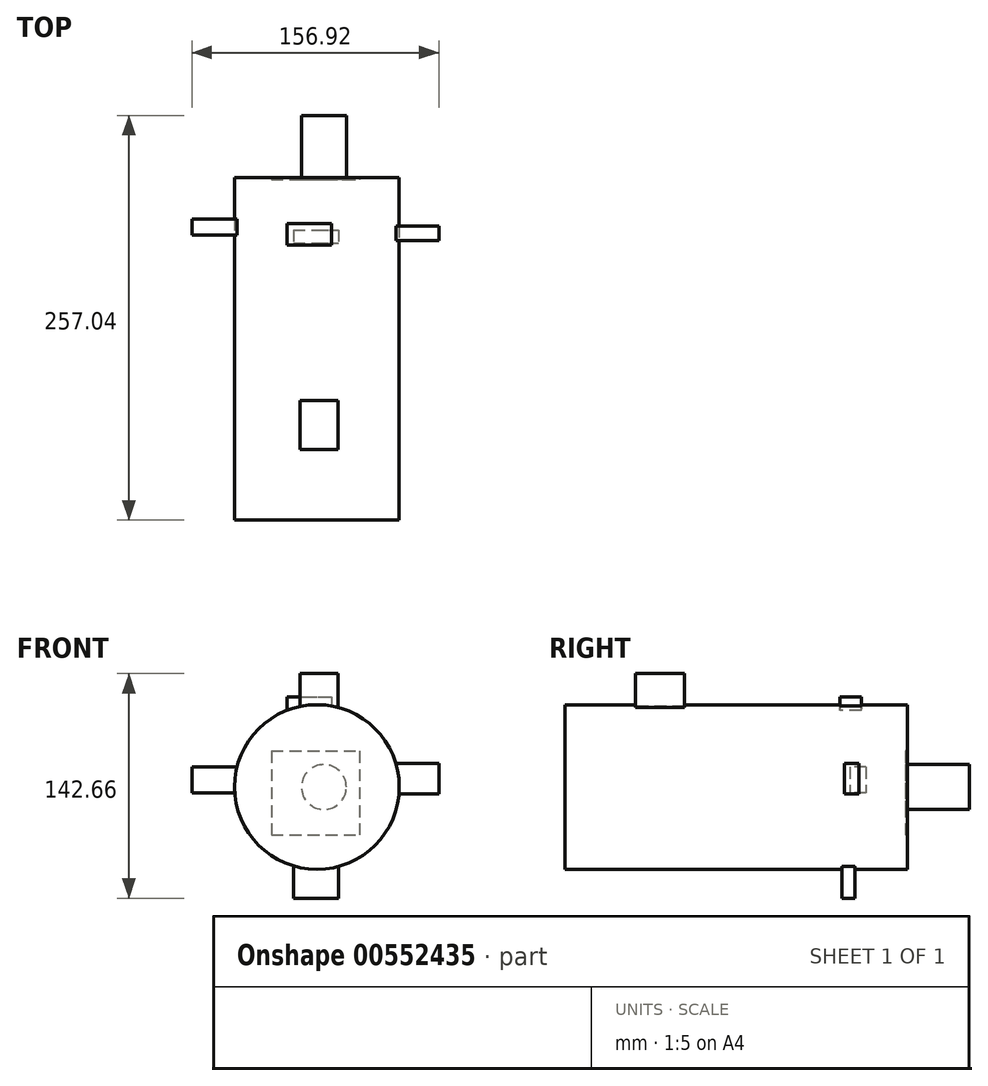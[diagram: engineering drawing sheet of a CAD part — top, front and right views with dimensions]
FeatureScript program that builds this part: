
annotation { "Feature Type Name" : "Feature", "Feature Type Description" : "" }
export const myFeature = defineFeature(function(context is Context, id is Id, definition is map)
    precondition{}
    {
        {
            var Q0;
            Q0=qCreatedBy(makeId("Front.planeOp"),FACE);
            var sketch = newSketch(context, id + "F0", { "sketchPlane" : qUnion([Q0])});
            skLineSegment(sketch, "E0.bottom", {"start": v(-9.91, 22.8) * mm, "end": v(46.17, 22.8) * mm});
            skLineSegment(sketch, "E0.top", {"start": v(-9.91, -30.45) * mm, "end": v(46.17, -30.45) * mm});
            skLineSegment(sketch, "E0.left", {"start": v(-9.91, 22.8) * mm, "end": v(-9.91, -30.45) * mm});
            skLineSegment(sketch, "E0.right", {"start": v(46.17, 22.8) * mm, "end": v(46.17, -30.45) * mm});
            skSolve(sketch);
        }
        {
            var Q0;
            Q0 = qSketchRegion(id + "F0", true);
            extrude(context, id + "F1", {"entities" : qUnion([Q0]), "depth" : 44.7 * mm, "offsetDistance" : 25.4 * mm});
        }
        {
            var Q0;
            Q0=makeQuery(id+"F1.opExtrude","CAP_FACE",FACE,{"disambiguationData":[OSD([sQuery(id+"F0.wireOp",EDGE,"E0.bottom"),sQuery(id+"F0.wireOp",EDGE,"E0.top"),sQuery(id+"F0.wireOp",EDGE,"E0.left"),sQuery(id+"F0.wireOp",EDGE,"E0.right")])],"isStart":true});
            extrude(context, id + "F2", {"entities" : qUnion([Q0]), "operationType" : NewBodyOperationType.ADD, "depth" : 156.46 * mm, "offsetDistance" : 25.4 * mm});
        }
        {
            var Q0;
            {var subQ0=sQuery(id+"F0.wireOp",EDGE,"E0.bottom");Q0=makeQuery(id+"F2.boolean.opBoolean","MERGE",FACE,{"derivedFrom":[makeQuery(id+"F1.opExtrude","SWEPT_FACE",FACE,{"disambiguationData":[OSD([subQ0])]}),makeQuery(id+"F2.opExtrude","SWEPT_FACE",FACE,{"disambiguationData":[OSD([subQ0])]})]});}
            var sketch = newSketch(context, id + "F3", { "sketchPlane" : qUnion([Q0])});
            skLineSegment(sketch, "E1", {"start": v(32.43, 0) * mm, "end": v(8.22, 0) * mm});
            skLineSegment(sketch, "E2", {"start": v(8.22, 0) * mm, "end": v(8.22, 31.27) * mm});
            skLineSegment(sketch, "E3", {"start": v(8.22, 31.27) * mm, "end": v(32.43, 31.27) * mm});
            skLineSegment(sketch, "E4", {"start": v(32.43, 31.27) * mm, "end": v(32.43, 0) * mm});
            skSolve(sketch);
        }
        {
            var Q0;
            Q0 = qSketchRegion(id + "F3", true);
            extrude(context, id + "F4", {"entities" : qUnion([Q0]), "operationType" : NewBodyOperationType.ADD, "depth" : 49.28 * mm, "offsetDistance" : 25.4 * mm});
        }
        {
            var Q0;
            Q0=makeQuery(id+"F1.opExtrude","CAP_FACE",FACE,{"disambiguationData":[OSD([sQuery(id+"F0.wireOp",EDGE,"E0.bottom"),sQuery(id+"F0.wireOp",EDGE,"E0.top"),sQuery(id+"F0.wireOp",EDGE,"E0.left"),sQuery(id+"F0.wireOp",EDGE,"E0.right")])],"isStart":false});
            var sketch = newSketch(context, id + "F5", { "sketchPlane" : qUnion([Q0])});
            skCircle(sketch, "E5", {"center": v(18.98, 0) * mm, "radius": 52.3 * mm});
            skSolve(sketch);
        }
        {
            var Q0;
            Q0 = qSketchRegion(id + "F5", true);
            extrude(context, id + "F6", {"entities" : qUnion([Q0]), "operationType" : NewBodyOperationType.ADD, "oppositeDirection" : true, "depth" : 167.39 * mm, "offsetDistance" : 25.4 * mm});
        }
        {
            var Q0;
            {var subQ0=sQuery(id+"F0.wireOp",EDGE,"E0.bottom");Q0=makeQuery(id+"F2.boolean.opBoolean","MERGE",FACE,{"derivedFrom":[makeQuery(id+"F1.opExtrude","SWEPT_FACE",FACE,{"disambiguationData":[OSD([subQ0])]}),makeQuery(id+"F2.opExtrude","SWEPT_FACE",FACE,{"disambiguationData":[OSD([subQ0])]})]});}
            var sketch = newSketch(context, id + "F7", { "sketchPlane" : qUnion([Q0])});
            skLineSegment(sketch, "E6.bottom", {"start": v(0, 143.52) * mm, "end": v(28.28, 143.52) * mm});
            skLineSegment(sketch, "E6.top", {"start": v(0, 130.11) * mm, "end": v(28.28, 130.11) * mm});
            skLineSegment(sketch, "E6.left", {"start": v(0, 143.52) * mm, "end": v(0, 130.11) * mm});
            skLineSegment(sketch, "E6.right", {"start": v(28.28, 143.52) * mm, "end": v(28.28, 130.11) * mm});
            skSolve(sketch);
        }
        {
            var Q0;
            Q0 = qSketchRegion(id + "F7", true);
            extrude(context, id + "F8", {"entities" : qUnion([Q0]), "operationType" : NewBodyOperationType.ADD, "depth" : 34.3 * mm, "offsetDistance" : 25.4 * mm});
        }
        {
            var Q0;
            {var subQ0=sQuery(id+"F0.wireOp",EDGE,"E0.right");Q0=makeQuery(id+"F2.boolean.opBoolean","MERGE",FACE,{"derivedFrom":[makeQuery(id+"F1.opExtrude","SWEPT_FACE",FACE,{"disambiguationData":[OSD([subQ0])]}),makeQuery(id+"F2.opExtrude","SWEPT_FACE",FACE,{"disambiguationData":[OSD([subQ0])]})]});}
            var sketch = newSketch(context, id + "F9", { "sketchPlane" : qUnion([Q0])});
            skLineSegment(sketch, "E7.bottom", {"start": v(142.1, 14.87) * mm, "end": v(132.75, 14.87) * mm});
            skLineSegment(sketch, "E7.top", {"start": v(142.1, -4.39) * mm, "end": v(132.75, -4.39) * mm});
            skLineSegment(sketch, "E7.left", {"start": v(142.1, 14.87) * mm, "end": v(142.1, -4.39) * mm});
            skLineSegment(sketch, "E7.right", {"start": v(132.75, 14.87) * mm, "end": v(132.75, -4.39) * mm});
            skSolve(sketch);
        }
        {
            var Q0;
            Q0 = qSketchRegion(id + "F9", true);
            extrude(context, id + "F10", {"entities" : qUnion([Q0]), "operationType" : NewBodyOperationType.ADD, "depth" : 50.3 * mm, "offsetDistance" : 25.4 * mm});
        }
        {
            var Q0;
            {var subQ0=sQuery(id+"F0.wireOp",EDGE,"E0.left");Q0=makeQuery(id+"F2.boolean.opBoolean","MERGE",FACE,{"derivedFrom":[makeQuery(id+"F1.opExtrude","SWEPT_FACE",FACE,{"disambiguationData":[OSD([subQ0])]}),makeQuery(id+"F2.opExtrude","SWEPT_FACE",FACE,{"disambiguationData":[OSD([subQ0])]})]});}
            var sketch = newSketch(context, id + "F11", { "sketchPlane" : qUnion([Q0])});
            skPoint(sketch, "E8.oppositeSnap0", {"position": v(-156.46, -3.82) * mm});
            skLineSegment(sketch, "E8.bottom", {"start": v(-136.37, 12.76) * mm, "end": v(-146.63, 12.76) * mm});
            skLineSegment(sketch, "E8.top", {"start": v(-136.37, -3.82) * mm, "end": v(-146.63, -3.82) * mm});
            skLineSegment(sketch, "E8.left", {"start": v(-136.37, 12.76) * mm, "end": v(-136.37, -3.82) * mm});
            skLineSegment(sketch, "E8.right", {"start": v(-146.63, 12.76) * mm, "end": v(-146.63, -3.82) * mm});
            skSolve(sketch);
        }
        {
            var Q0;
            Q0 = qSketchRegion(id + "F11", true);
            extrude(context, id + "F12", {"entities" : qUnion([Q0]), "operationType" : NewBodyOperationType.ADD, "depth" : 50.55 * mm, "offsetDistance" : 25.4 * mm});
        }
        {
            var Q0;
            {var subQ0=sQuery(id+"F0.wireOp",EDGE,"E0.top");Q0=makeQuery(id+"F2.boolean.opBoolean","MERGE",FACE,{"derivedFrom":[makeQuery(id+"F1.opExtrude","SWEPT_FACE",FACE,{"disambiguationData":[OSD([subQ0])]}),makeQuery(id+"F2.opExtrude","SWEPT_FACE",FACE,{"disambiguationData":[OSD([subQ0])]})]});}
            var sketch = newSketch(context, id + "F13", { "sketchPlane" : qUnion([Q0])});
            skPoint(sketch, "E9.firstSnap0", {"position": v(46.17, -139.57) * mm});
            skLineSegment(sketch, "E9.bottom", {"start": v(3.98, -139.57) * mm, "end": v(32.72, -139.57) * mm});
            skLineSegment(sketch, "E9.top", {"start": v(3.98, -131.24) * mm, "end": v(32.72, -131.24) * mm});
            skLineSegment(sketch, "E9.left", {"start": v(3.98, -139.57) * mm, "end": v(3.98, -131.24) * mm});
            skLineSegment(sketch, "E9.right", {"start": v(32.72, -139.57) * mm, "end": v(32.72, -131.24) * mm});
            skSolve(sketch);
        }
        {
            var Q0;
            Q0 = qSketchRegion(id + "F13", true);
            extrude(context, id + "F14", {"entities" : qUnion([Q0]), "operationType" : NewBodyOperationType.ADD, "depth" : 40.13 * mm, "offsetDistance" : 25.4 * mm});
        }
        {
            var Q0;
            Q0=makeQuery(id+"F6.opExtrude","CAP_FACE",FACE,{"disambiguationData":[OSD([sQuery(id+"F5.wireOp",EDGE,"E5")])],"isStart":false});
            extrude(context, id + "F15", {"entities" : qUnion([Q0]), "operationType" : NewBodyOperationType.ADD, "depth" : 50.3 * mm, "offsetDistance" : 25.4 * mm});
        }
        {
            var Q0;
            Q0=makeQuery(id+"F2.opExtrude","CAP_FACE",FACE,{"disambiguationData":[OSD([sQuery(id+"F0.wireOp",EDGE,"E0.bottom"),sQuery(id+"F0.wireOp",EDGE,"E0.top"),sQuery(id+"F0.wireOp",EDGE,"E0.left"),sQuery(id+"F0.wireOp",EDGE,"E0.right")])],"isStart":false});
            var sketch = newSketch(context, id + "F16", { "sketchPlane" : qUnion([Q0])});
            skLineSegment(sketch, "E10", {"start": v(-46.17, 22.8) * mm, "end": v(9.91, 22.8) * mm});
            skLineSegment(sketch, "E11", {"start": v(9.91, 22.8) * mm, "end": v(9.91, -30.45) * mm});
            skLineSegment(sketch, "E12", {"start": v(9.91, -30.45) * mm, "end": v(-46.17, -30.45) * mm});
            skLineSegment(sketch, "E13", {"start": v(-46.17, -30.45) * mm, "end": v(-46.17, 22.8) * mm});
            skSolve(sketch);
        }
        {
            var Q0;
            Q0 = qSketchRegion(id + "F16", true);
            extrude(context, id + "F17", {"entities" : qUnion([Q0]), "operationType" : NewBodyOperationType.ADD, "depth" : 15.24 * mm, "offsetDistance" : 25.4 * mm});
        }
        {
            var Q0;
            Q0=makeQuery(id+"F17.opExtrude","CAP_FACE",FACE,{"disambiguationData":[OSD([sQuery(id+"F16.wireOp",EDGE,"E10"),sQuery(id+"F16.wireOp",EDGE,"E11"),sQuery(id+"F16.wireOp",EDGE,"E12"),sQuery(id+"F16.wireOp",EDGE,"E13")])],"isStart":false});
            var sketch = newSketch(context, id + "F18", { "sketchPlane" : qUnion([Q0])});
            skCircle(sketch, "E14", {"center": v(-23.4, 0) * mm, "radius": 14.25 * mm});
            skSolve(sketch);
        }
        {
            var Q0;
            Q0 = qSketchRegion(id + "F18", true);
            extrude(context, id + "F19", {"entities" : qUnion([Q0]), "operationType" : NewBodyOperationType.ADD, "depth" : 40.64 * mm, "offsetDistance" : 25.4 * mm});
        }
    });
